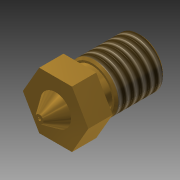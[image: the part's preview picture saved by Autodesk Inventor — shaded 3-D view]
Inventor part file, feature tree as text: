
AUTODESK INVENTOR PART (.ipt)
format: ipt  version: 2015 (Build 190159000, 159)  size: 147,456 bytes
history: native  units: mm
features: sketch x4, hole x3, chamfer x2, other x1, revolve x1, thread x1, extrude x1
ambient origin geometry x8: Origin, YZ Plane, XZ Plane, XY Plane, X Axis, Y Axis, Z Axis, Center Point
bodies: Body1 (feature_tree)
feature tree (13):
  other  "Твердое тело1"
  revolve  "Вращение1"
  chamfer  "Фаска1"  Distance=15.0mm
  thread  "Резьба1"
  sketch  "Эскиз2"
  sketch  "Эскиз3"
  hole  "Отверстие1"  [1 undecoded]
  hole  "Отверстие2"  [1 undecoded]
  hole  "Отверстие3"  [1 undecoded]
  extrude  "Выдавливание1"  Depth=6.0mm
  chamfer  "Фаска2"  Distance=0.5mm
  sketch  "Эскиз1"
  sketch  "Эскиз4"
note: 3 required parameter values undecoded (feature->parameter linkage not recoverable at this tier; creation-order binding heuristic only, values carry confidence <= 0.55)
